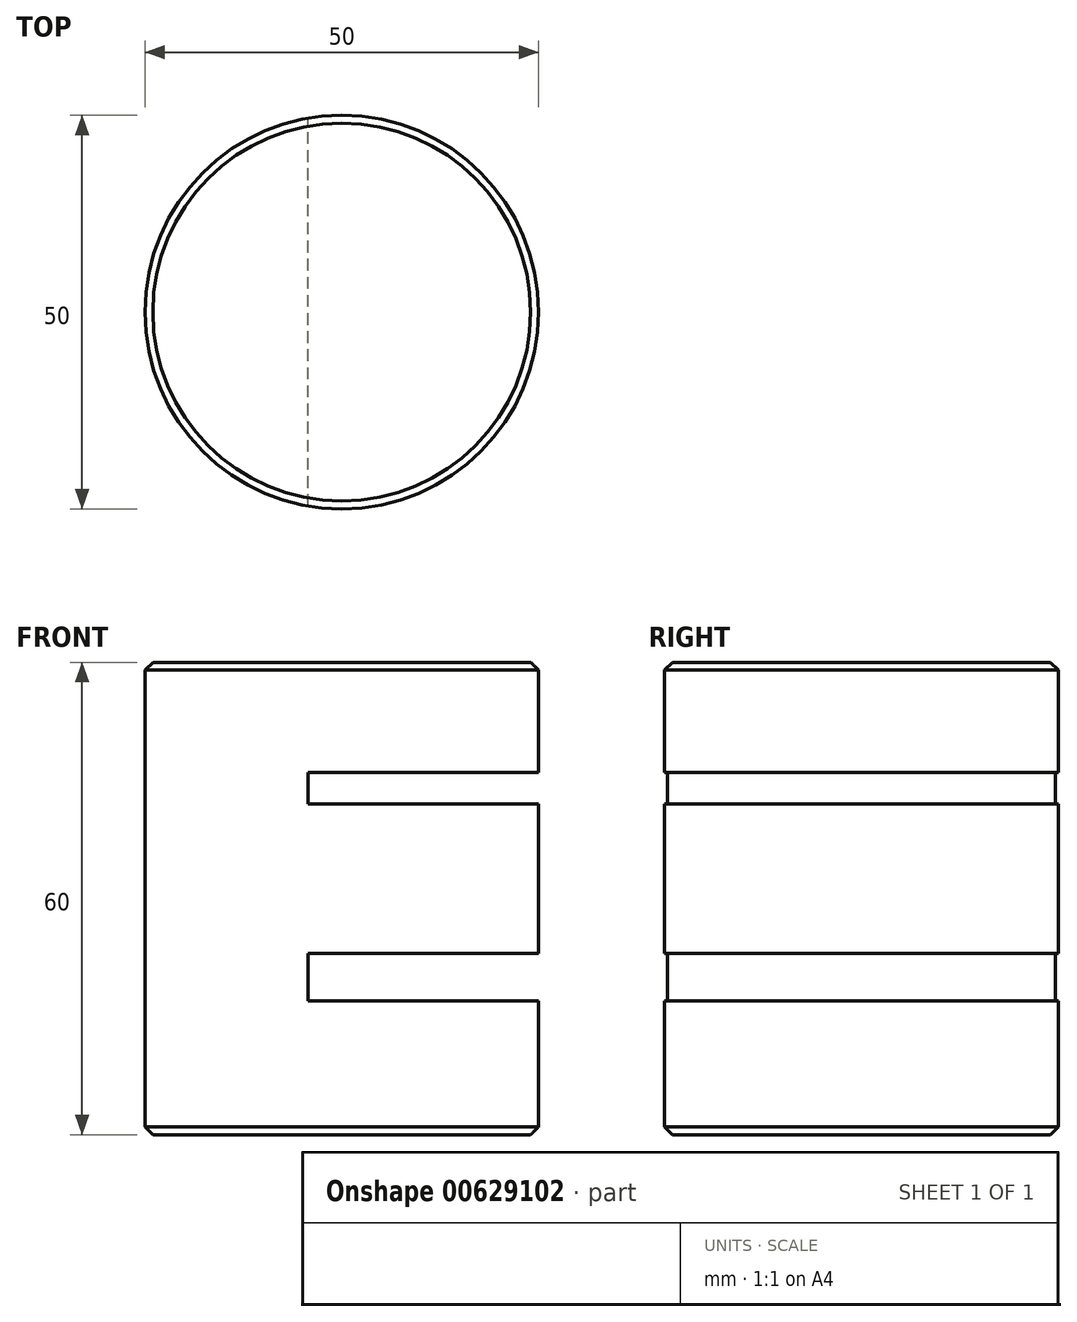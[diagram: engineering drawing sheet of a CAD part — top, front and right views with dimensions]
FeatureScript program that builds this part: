
annotation { "Feature Type Name" : "Feature", "Feature Type Description" : "" }
export const myFeature = defineFeature(function(context is Context, id is Id, definition is map)
    precondition{}
    {
        {
            var Q0;
            Q0=qCreatedBy(makeId("Top.planeOp"),FACE);
            var sketch = newSketch(context, id + "F0", { "sketchPlane" : qUnion([Q0])});
            skCircle(sketch, "E0", {"center": v(0, 0) * mm, "radius": 25 * mm});
            skSolve(sketch);
        }
        {
            var Q0;
            Q0 = qSketchRegion(id + "F0", true);
            extrude(context, id + "F1", {"entities" : qUnion([Q0]), "depth" : 60 * mm, "offsetDistance" : 25 * mm});
        }
        {
            var Q0;
            Q0=qCreatedBy(makeId("Top.planeOp"),FACE);
            var sketch = newSketch(context, id + "F2", { "sketchPlane" : qUnion([Q0])});
            skLineSegment(sketch, "E1.bottom", {"start": v(-130.72, -60.24) * mm, "end": v(-192.3, -60.24) * mm});
            skLineSegment(sketch, "E1.top", {"start": v(-130.72, 123.96) * mm, "end": v(-192.3, 123.96) * mm});
            skLineSegment(sketch, "E1.left", {"start": v(-130.72, -60.24) * mm, "end": v(-130.72, 123.96) * mm});
            skLineSegment(sketch, "E1.right", {"start": v(-192.3, -60.24) * mm, "end": v(-192.3, 123.96) * mm});
            skSolve(sketch);
        }
        {
            var Q0;
            Q0 = qSketchRegion(id + "F2", true);
            extrude(context, id + "F3", {"entities" : qUnion([Q0]), "depth" : 6 * mm, "offsetDistance" : 25 * mm});
        }
        {
            var Q0;
            Q0=makeQuery(id+"F3.opExtrude","SWEPT_BODY",BODY,{"disambiguationData":[OSD([sQuery(id+"F2.wireOp",EDGE,"E1.bottom"),sQuery(id+"F2.wireOp",EDGE,"E1.top"),sQuery(id+"F2.wireOp",EDGE,"E1.left"),sQuery(id+"F2.wireOp",EDGE,"E1.right")])]});
            transform(context, id + "F4", {"entities" : qUnion([Q0]), "transformType" : TransformType.TRANSLATION_3D, "dx" : 188 * mm, "dy" : 0 * mm, "dz" : 17 * mm, "makeCopy" : true});
        }
        {
            var Q0;
            Q0=makeQuery(id+"F4.opPattern","COPY",BODY,{"derivedFrom":makeQuery(id+"F3.opExtrude","SWEPT_BODY",BODY,{"disambiguationData":[OSD([sQuery(id+"F2.wireOp",EDGE,"E1.bottom"),sQuery(id+"F2.wireOp",EDGE,"E1.top"),sQuery(id+"F2.wireOp",EDGE,"E1.left"),sQuery(id+"F2.wireOp",EDGE,"E1.right")])]}),"instanceName":"1"});
            transform(context, id + "F5", {"entities" : qUnion([Q0]), "transformType" : TransformType.TRANSLATION_3D, "dx" : 0 * mm, "dy" : 0 * mm, "dz" : 17 * mm, "makeCopy" : true});
        }
        {
            var Q0;
            Q0=makeQuery(id+"F5.opPattern","COPY",BODY,{"derivedFrom":makeQuery(id+"F4.opPattern","COPY",BODY,{"derivedFrom":makeQuery(id+"F3.opExtrude","SWEPT_BODY",BODY,{"disambiguationData":[OSD([sQuery(id+"F2.wireOp",EDGE,"E1.bottom"),sQuery(id+"F2.wireOp",EDGE,"E1.top"),sQuery(id+"F2.wireOp",EDGE,"E1.left"),sQuery(id+"F2.wireOp",EDGE,"E1.right")])]}),"instanceName":"1"}),"instanceName":"1"});
            deleteBodies(context, id + "F6", {"entities" : qUnion([Q0])});
        }
        {
            var Q0;
            Q0=makeQuery(id+"F4.opPattern","COPY",BODY,{"derivedFrom":makeQuery(id+"F3.opExtrude","SWEPT_BODY",BODY,{"disambiguationData":[OSD([sQuery(id+"F2.wireOp",EDGE,"E1.bottom"),sQuery(id+"F2.wireOp",EDGE,"E1.top"),sQuery(id+"F2.wireOp",EDGE,"E1.left"),sQuery(id+"F2.wireOp",EDGE,"E1.right")])]}),"instanceName":"1"});
            transform(context, id + "F7", {"entities" : qUnion([Q0]), "transformType" : TransformType.TRANSLATION_3D, "dx" : 0 * mm, "dy" : 0 * mm, "dz" : 23 * mm, "makeCopy" : true});
        }
        {
            var Q0;
            Q0=makeQuery(id+"F4.opPattern","COPY",BODY,{"derivedFrom":makeQuery(id+"F3.opExtrude","SWEPT_BODY",BODY,{"disambiguationData":[OSD([sQuery(id+"F2.wireOp",EDGE,"E1.bottom"),sQuery(id+"F2.wireOp",EDGE,"E1.top"),sQuery(id+"F2.wireOp",EDGE,"E1.left"),sQuery(id+"F2.wireOp",EDGE,"E1.right")])]}),"instanceName":"1"});
            var Q1;
            Q1=makeQuery(id+"F7.opPattern","COPY",BODY,{"derivedFrom":makeQuery(id+"F4.opPattern","COPY",BODY,{"derivedFrom":makeQuery(id+"F3.opExtrude","SWEPT_BODY",BODY,{"disambiguationData":[OSD([sQuery(id+"F2.wireOp",EDGE,"E1.bottom"),sQuery(id+"F2.wireOp",EDGE,"E1.top"),sQuery(id+"F2.wireOp",EDGE,"E1.left"),sQuery(id+"F2.wireOp",EDGE,"E1.right")])]}),"instanceName":"1"}),"instanceName":"1"});
            var Q2;
            Q2=makeQuery(id+"F1.opExtrude","SWEPT_BODY",BODY,{"disambiguationData":[OSD([sQuery(id+"F0.wireOp",EDGE,"E0")])]});
            booleanBodies(context, id + "F8", {"operationType" : BooleanOperationType.SUBTRACTION, "tools" : qUnion([Q0, Q1]), "targets" : qUnion([Q2])});
        }
        {
            var Q0;
            Q0=makeQuery(id+"F3.opExtrude","SWEPT_BODY",BODY,{"disambiguationData":[OSD([sQuery(id+"F2.wireOp",EDGE,"E1.bottom"),sQuery(id+"F2.wireOp",EDGE,"E1.top"),sQuery(id+"F2.wireOp",EDGE,"E1.left"),sQuery(id+"F2.wireOp",EDGE,"E1.right")])]});
            deleteBodies(context, id + "F9", {"entities" : qUnion([Q0])});
        }
        {
            var Q0;
            Q0=makeQuery(id+"F1.opExtrude","CAP_EDGE",EDGE,{"disambiguationData":[OSD([sQuery(id+"F0.wireOp",EDGE,"E0")])],"isStart":false});
            chamfer(context, id + "F10", {"entities" : qUnion([Q0]), "width" : 1 * mm, "tangentPropagation" : true});
        }
        {
            var Q0;
            Q0=makeQuery(id+"F1.opExtrude","CAP_EDGE",EDGE,{"disambiguationData":[OSD([sQuery(id+"F0.wireOp",EDGE,"E0")])],"isStart":true});
            chamfer(context, id + "F11", {"entities" : qUnion([Q0]), "width" : 1 * mm, "tangentPropagation" : true});
        }
        {
            var Q0;
            Q0=makeQuery(id+"F8.opBoolean","COPY",FACE,{"derivedFrom":makeQuery(id+"F7.opPattern","COPY",FACE,{"derivedFrom":makeQuery(id+"F4.opPattern","COPY",FACE,{"derivedFrom":makeQuery(id+"F3.opExtrude","CAP_FACE",FACE,{"disambiguationData":[OSD([sQuery(id+"F2.wireOp",EDGE,"E1.bottom"),sQuery(id+"F2.wireOp",EDGE,"E1.top"),sQuery(id+"F2.wireOp",EDGE,"E1.left"),sQuery(id+"F2.wireOp",EDGE,"E1.right")])],"isStart":true}),"instanceName":"1"}),"instanceName":"1"})});
            extrude(context, id + "F12", {"entities" : qUnion([Q0]), "operationType" : NewBodyOperationType.ADD, "depth" : 2 * mm, "offsetDistance" : 25 * mm});
        }
    });
